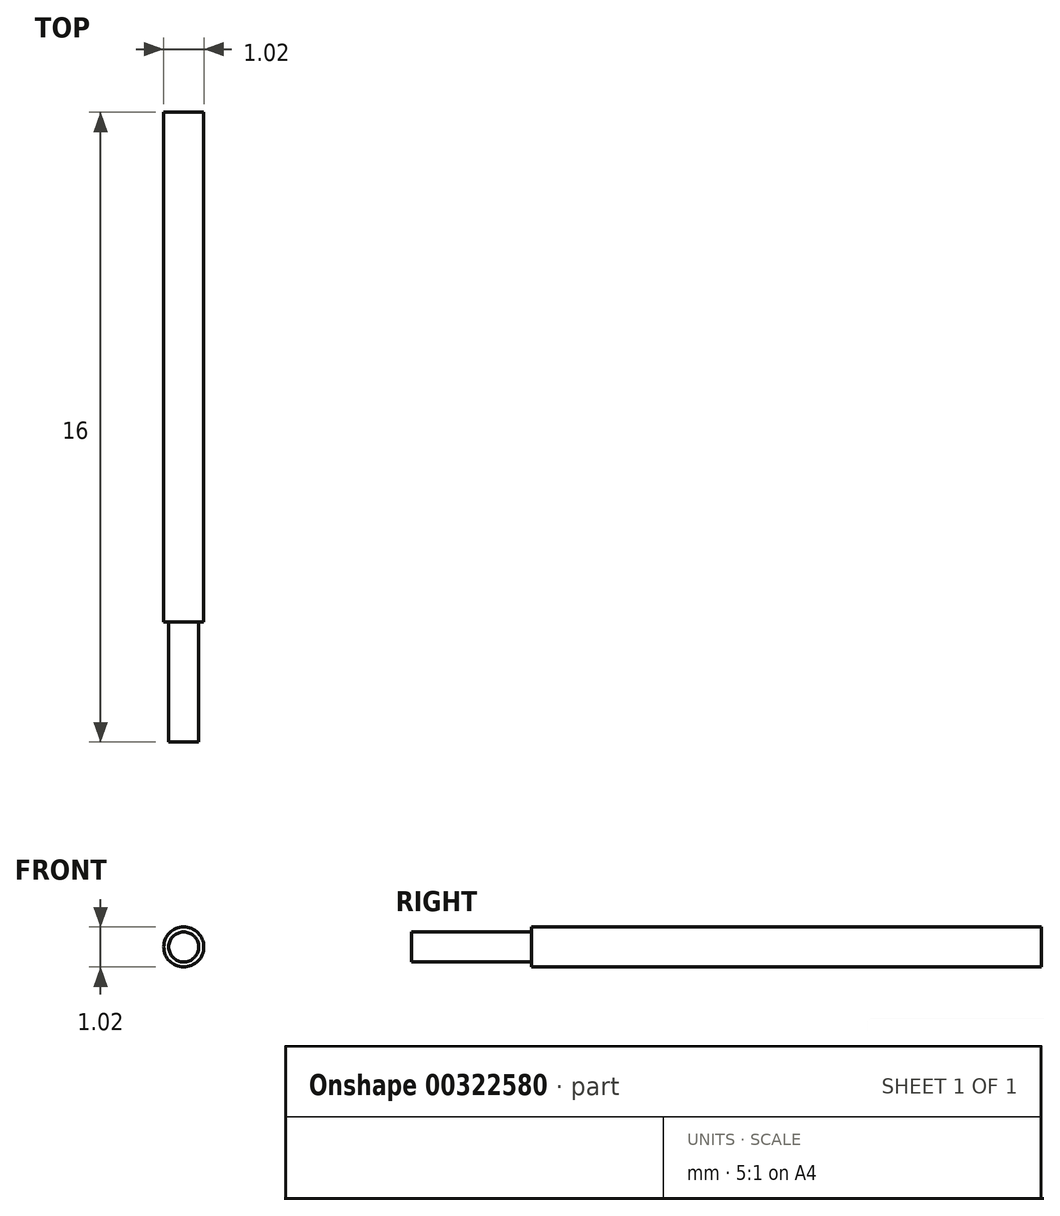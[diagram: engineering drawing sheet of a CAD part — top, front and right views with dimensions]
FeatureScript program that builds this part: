
annotation { "Feature Type Name" : "Feature", "Feature Type Description" : "" }
export const myFeature = defineFeature(function(context is Context, id is Id, definition is map)
    precondition{}
    {
        {
            var Q0;
            Q0=qCreatedBy(makeId("Front.planeOp"),FACE);
            var sketch = newSketch(context, id + "F0", { "sketchPlane" : qUnion([Q0])});
            skCircle(sketch, "E0", {"center": v(0, 0) * mm, "radius": 0.5 * mm});
            skSolve(sketch);
        }
        {
            var Q0;
            Q0 = qSketchRegion(id + "F0", true);
            extrude(context, id + "F1", {"entities" : qUnion([Q0]), "depth" : 12.95 * mm, "offsetDistance" : 25.4 * mm});
        }
        {
            var Q0;
            Q0=makeQuery(id+"F1.opExtrude","CAP_FACE",FACE,{"disambiguationData":[OSD([sQuery(id+"F0.wireOp",EDGE,"E0")])],"isStart":false});
            var sketch = newSketch(context, id + "F2", { "sketchPlane" : qUnion([Q0])});
            skCircle(sketch, "E1", {"center": v(0, 0) * mm, "radius": 0.38 * mm});
            skSolve(sketch);
        }
        {
            var Q0;
            Q0 = qSketchRegion(id + "F2", true);
            extrude(context, id + "F3", {"entities" : qUnion([Q0]), "operationType" : NewBodyOperationType.ADD, "depth" : 3.05 * mm, "offsetDistance" : 25.4 * mm});
        }
    });
